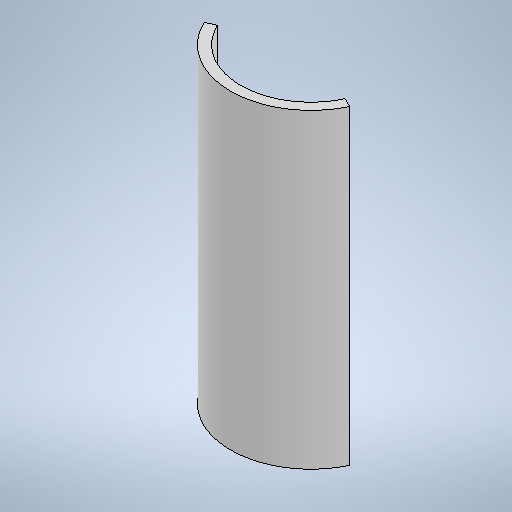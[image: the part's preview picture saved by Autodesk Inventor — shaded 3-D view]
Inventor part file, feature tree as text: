
AUTODESK INVENTOR PART (.ipt)
format: ipt  version: 2025.1 (Build 291241020, 241B)  size: 235,520 bytes
history: native  units: mm
features: extrude x2, sketch x2, projected_geometry x1
ambient origin geometry x8: Origin, YZ Plane, XZ Plane, XY Plane, X Axis, Y Axis, Z Axis, Center Point
bodies: Solid1 (feature_tree)
feature tree (5):
  extrude  "Extrusion1"  Depth=10.0mm
  extrude  "Extrusion3"  Depth=10.0mm TaperAngle=0.0deg
  sketch  "Sketch1"  dims[d2=310.0mm d3=0.0mm d6=10.0mm]
  sketch  "Sketch5"  dims[d8=22.68928mm d9=10.0mm d10=0.0mm d11=160.0mm]
  projected_geometry  "Projected Loop2"
